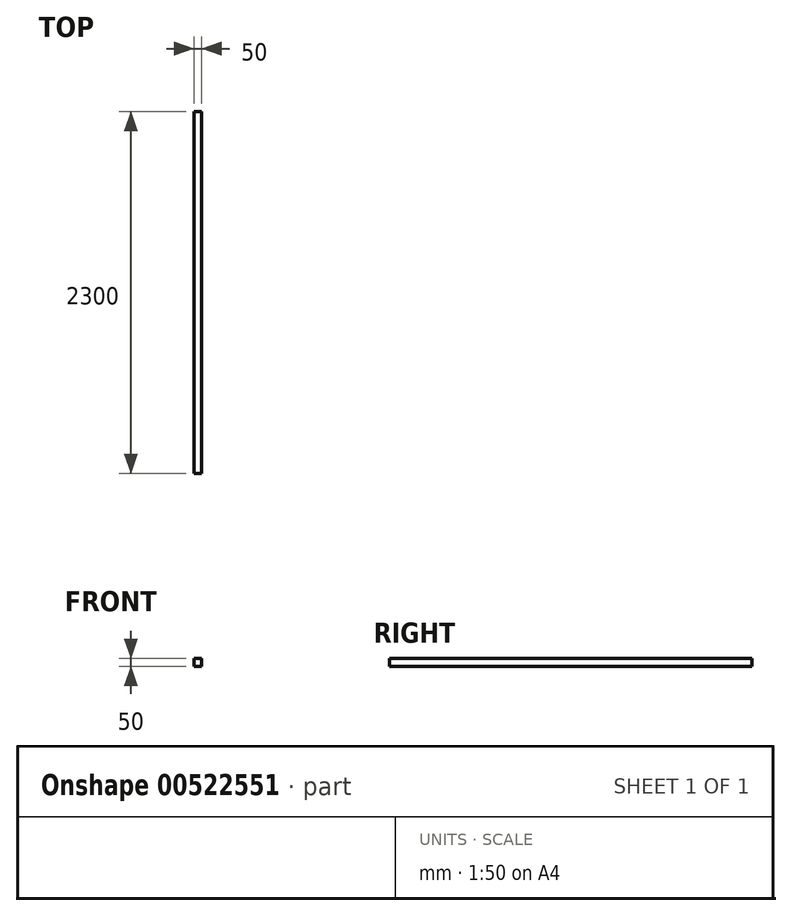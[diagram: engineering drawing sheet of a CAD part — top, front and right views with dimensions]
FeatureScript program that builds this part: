
annotation { "Feature Type Name" : "Feature", "Feature Type Description" : "" }
export const myFeature = defineFeature(function(context is Context, id is Id, definition is map)
    precondition{}
    {
        {
            var Q0;
            Q0=qCreatedBy(makeId("Front.planeOp"),FACE);
            var sketch = newSketch(context, id + "F0", { "sketchPlane" : qUnion([Q0])});
            skLineSegment(sketch, "E0.bottom", {"start": v(0, 0) * mm, "end": v(-50, 0) * mm});
            skLineSegment(sketch, "E0.top", {"start": v(0, 50) * mm, "end": v(-50, 50) * mm});
            skLineSegment(sketch, "E0.left", {"start": v(0, 0) * mm, "end": v(0, 50) * mm});
            skLineSegment(sketch, "E0.right", {"start": v(-50, 0) * mm, "end": v(-50, 50) * mm});
            skSolve(sketch);
        }
        {
            var Q0;
            Q0 = qSketchRegion(id + "F0", true);
            extrude(context, id + "F1", {"entities" : qUnion([Q0]), "depth" : 2300 * mm, "offsetDistance" : 25 * mm});
        }
    });
